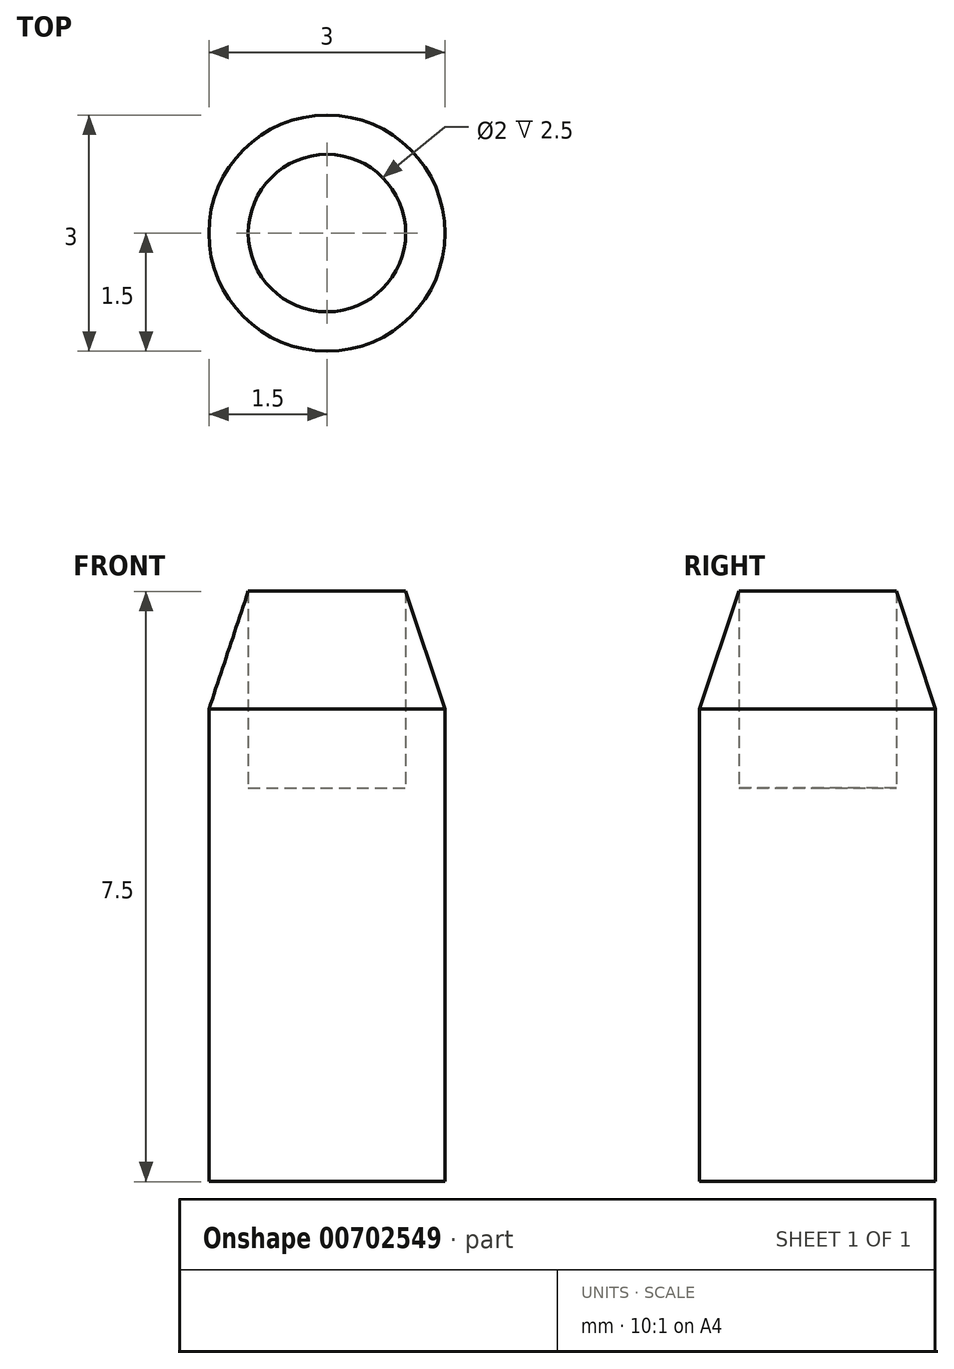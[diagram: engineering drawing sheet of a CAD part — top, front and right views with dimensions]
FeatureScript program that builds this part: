
annotation { "Feature Type Name" : "Feature", "Feature Type Description" : "" }
export const myFeature = defineFeature(function(context is Context, id is Id, definition is map)
    precondition{}
    {
        {
            var Q0;
            Q0=qCreatedBy(makeId("Front.planeOp"),FACE);
            var sketch = newSketch(context, id + "F0", { "sketchPlane" : qUnion([Q0])});
            skLineSegment(sketch, "E0", {"start": v(0, 4.28) * mm, "end": v(1, 4.28) * mm});
            skLineSegment(sketch, "E1", {"start": v(1, 4.28) * mm, "end": v(1, 6.78) * mm});
            skLineSegment(sketch, "E2", {"start": v(1, 6.78) * mm, "end": v(1.5, 5.28) * mm});
            skLineSegment(sketch, "E3", {"start": v(1.5, 5.28) * mm, "end": v(1.5, -0.72) * mm});
            skLineSegment(sketch, "E4", {"start": v(1.5, -0.72) * mm, "end": v(0, -0.72) * mm});
            skLineSegment(sketch, "E5", {"start": v(0, -0.72) * mm, "end": v(0, 4.28) * mm});
            skSolve(sketch);
        }
        {
            var Q0;
            Q0=makeQuery(id+"F0.imprint","IMPRINT",FACE,{"disambiguationData":[TD([[makeQuery(id+"F0.imprint","IMPRINT",EDGE,{"derivedFrom":sQuery(id+"F0.wireOp",EDGE,"E0")}),-1.0]])]});
            var Q1;
            Q1=sQuery(id+"F0.wireOp",EDGE,"E5");
            revolve(context, id + "F1", {"entities" : qUnion([Q0]), "axis" : qUnion([Q1]), "revolveType" : RevolveType.FULL});
        }
    });
